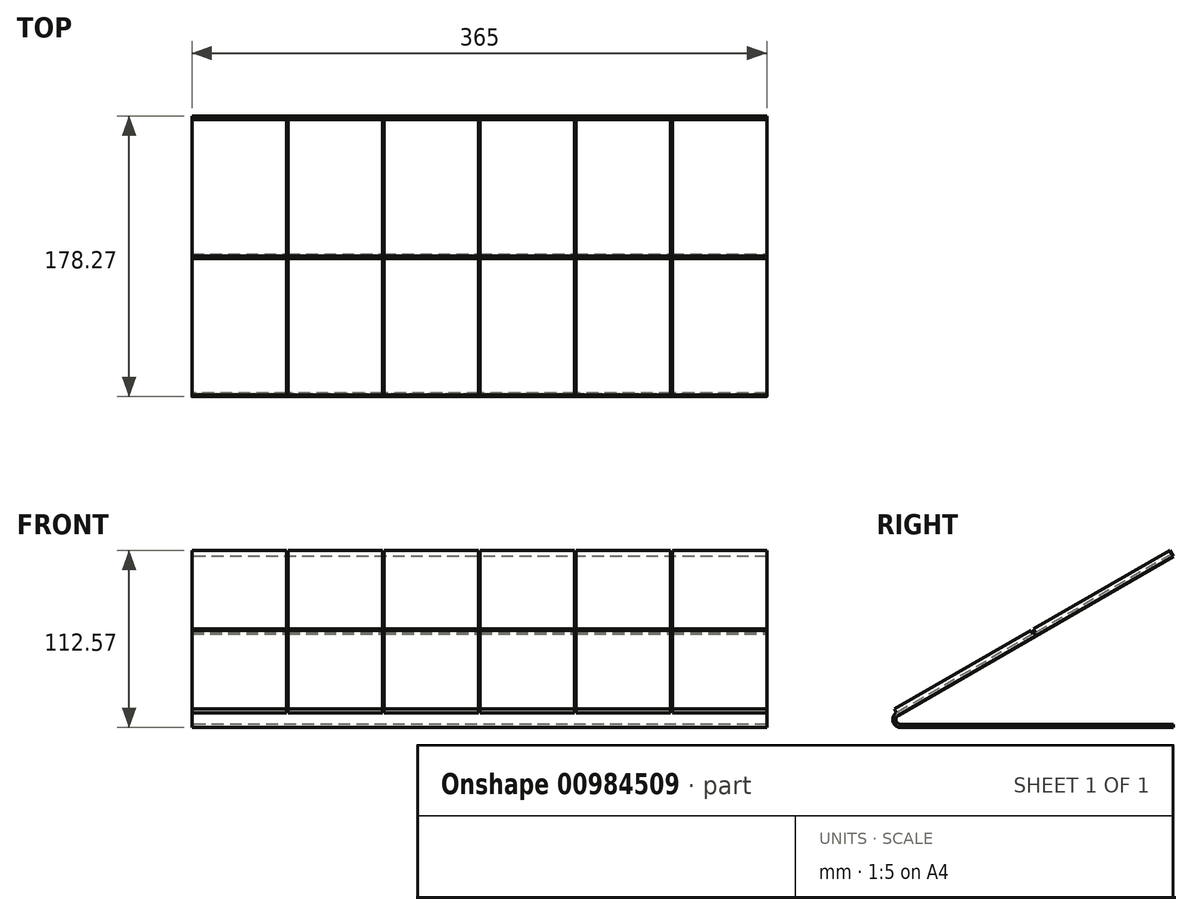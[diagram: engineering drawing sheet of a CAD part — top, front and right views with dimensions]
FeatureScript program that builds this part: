
annotation { "Feature Type Name" : "Feature", "Feature Type Description" : "" }
export const myFeature = defineFeature(function(context is Context, id is Id, definition is map)
    precondition{}
    {
        {
            var Q0;
            Q0=qCreatedBy(makeId("Right.planeOp"),FACE);
            var sketch = newSketch(context, id + "F0", { "sketchPlane" : qUnion([Q0])});
            skLineSegment(sketch, "E0", {"start": v(0, 2) * mm, "end": v(-184.46, 2) * mm});
            skLineSegment(sketch, "E1", {"start": v(-184.46, 2) * mm, "end": v(0, 108.5) * mm});
            skLineSegment(sketch, "E2", {"start": v(0, 108.5) * mm, "end": v(-1, 110.23) * mm});
            skLineSegment(sketch, "E3", {"start": v(-1, 110.23) * mm, "end": v(-191.93, 0) * mm});
            skLineSegment(sketch, "E4", {"start": v(-191.93, 0) * mm, "end": v(0, 0) * mm});
            skLineSegment(sketch, "E5", {"start": v(0, 0) * mm, "end": v(0, 2) * mm});
            skSolve(sketch);
        }
        {
            var Q0;
            Q0 = qSketchRegion(id + "F0", true);
            extrude(context, id + "F1", {"entities" : qUnion([Q0]), "depth" : 365 * mm, "offsetDistance" : 25 * mm});
        }
        {
            var Q0;
            Q0=makeQuery(id+"F1.opExtrude","SWEPT_EDGE",EDGE,{"disambiguationData":[OSD([sQuery(id+"F0.wireOp",EDGE,"E0"),sQuery(id+"F0.wireOp",EDGE,"E1")])]});
            fillet(context, id + "F2", {"entities" : qUnion([Q0]), "radius" : 3 * mm, "tangentPropagation" : true, "allowEdgeOverflow" : false});
        }
        {
            var Q0;
            Q0=makeQuery(id+"F1.opExtrude","SWEPT_EDGE",EDGE,{"disambiguationData":[OSD([sQuery(id+"F0.wireOp",EDGE,"E3"),sQuery(id+"F0.wireOp",EDGE,"E4")])]});
            fillet(context, id + "F3", {"entities" : qUnion([Q0]), "radius" : 5 * mm, "tangentPropagation" : true, "allowEdgeOverflow" : false});
        }
        {
            var Q0;
            Q0=makeQuery(id+"F1.opExtrude","SWEPT_FACE",FACE,{"disambiguationData":[OSD([sQuery(id+"F0.wireOp",EDGE,"E3")])]});
            var sketch = newSketch(context, id + "F4", { "sketchPlane" : qUnion([Q0])});
            skLineSegment(sketch, "E6.bottom", {"start": v(0, 54.25) * mm, "end": v(60, 54.25) * mm});
            skLineSegment(sketch, "E6.top", {"start": v(0, -45.75) * mm, "end": v(60, -45.75) * mm});
            skLineSegment(sketch, "E6.left", {"start": v(0, 54.25) * mm, "end": v(0, -45.75) * mm});
            skLineSegment(sketch, "E6.right", {"start": v(60, 54.25) * mm, "end": v(60, -45.75) * mm});
            skLineSegment(sketch, "E7.bottom", {"start": v(61, 54.25) * mm, "end": v(121, 54.25) * mm});
            skLineSegment(sketch, "E7.top", {"start": v(61, -45.75) * mm, "end": v(121, -45.75) * mm});
            skLineSegment(sketch, "E7.left", {"start": v(61, 54.25) * mm, "end": v(61, -45.75) * mm});
            skLineSegment(sketch, "E7.right", {"start": v(121, 54.25) * mm, "end": v(121, -45.75) * mm});
            skLineSegment(sketch, "E8.bottom", {"start": v(122, 54.25) * mm, "end": v(182, 54.25) * mm});
            skLineSegment(sketch, "E8.top", {"start": v(122, -45.75) * mm, "end": v(182, -45.75) * mm});
            skLineSegment(sketch, "E8.left", {"start": v(122, 54.25) * mm, "end": v(122, -45.75) * mm});
            skLineSegment(sketch, "E8.right", {"start": v(182, 54.25) * mm, "end": v(182, -45.75) * mm});
            skLineSegment(sketch, "E9.bottom", {"start": v(183, 54.25) * mm, "end": v(243, 54.25) * mm});
            skLineSegment(sketch, "E9.top", {"start": v(183, -45.75) * mm, "end": v(243, -45.75) * mm});
            skLineSegment(sketch, "E9.left", {"start": v(183, 54.25) * mm, "end": v(183, -45.75) * mm});
            skLineSegment(sketch, "E9.right", {"start": v(243, 54.25) * mm, "end": v(243, -45.75) * mm});
            skLineSegment(sketch, "E10.bottom", {"start": v(244, 54.25) * mm, "end": v(304, 54.25) * mm});
            skLineSegment(sketch, "E10.top", {"start": v(244, -45.75) * mm, "end": v(304, -45.75) * mm});
            skLineSegment(sketch, "E10.left", {"start": v(244, 54.25) * mm, "end": v(244, -45.75) * mm});
            skLineSegment(sketch, "E10.right", {"start": v(304, 54.25) * mm, "end": v(304, -45.75) * mm});
            skLineSegment(sketch, "E11.bottom", {"start": v(305, 54.25) * mm, "end": v(365, 54.25) * mm});
            skLineSegment(sketch, "E11.top", {"start": v(305, -45.75) * mm, "end": v(365, -45.75) * mm});
            skLineSegment(sketch, "E11.left", {"start": v(305, 54.25) * mm, "end": v(305, -45.75) * mm});
            skLineSegment(sketch, "E11.right", {"start": v(365, 54.25) * mm, "end": v(365, -45.75) * mm});
            skLineSegment(sketch, "E12.bottom", {"start": v(0, -47.55) * mm, "end": v(60, -47.55) * mm});
            skLineSegment(sketch, "E12.top", {"start": v(0, -147.55) * mm, "end": v(60, -147.55) * mm});
            skLineSegment(sketch, "E12.left", {"start": v(0, -47.55) * mm, "end": v(0, -147.55) * mm});
            skLineSegment(sketch, "E12.right", {"start": v(60, -47.55) * mm, "end": v(60, -147.55) * mm});
            skLineSegment(sketch, "E13.bottom", {"start": v(61, -47.55) * mm, "end": v(121, -47.55) * mm});
            skLineSegment(sketch, "E13.top", {"start": v(61, -147.55) * mm, "end": v(121, -147.55) * mm});
            skLineSegment(sketch, "E13.left", {"start": v(61, -47.55) * mm, "end": v(61, -147.55) * mm});
            skLineSegment(sketch, "E13.right", {"start": v(121, -47.55) * mm, "end": v(121, -147.55) * mm});
            skLineSegment(sketch, "E14.bottom", {"start": v(122, -47.55) * mm, "end": v(182, -47.55) * mm});
            skLineSegment(sketch, "E14.top", {"start": v(122, -147.55) * mm, "end": v(182, -147.55) * mm});
            skLineSegment(sketch, "E14.left", {"start": v(122, -47.55) * mm, "end": v(122, -147.55) * mm});
            skLineSegment(sketch, "E14.right", {"start": v(182, -47.55) * mm, "end": v(182, -147.55) * mm});
            skLineSegment(sketch, "E15.bottom", {"start": v(183, -47.55) * mm, "end": v(243, -47.55) * mm});
            skLineSegment(sketch, "E15.top", {"start": v(183, -147.55) * mm, "end": v(243, -147.55) * mm});
            skLineSegment(sketch, "E15.left", {"start": v(183, -47.55) * mm, "end": v(183, -147.55) * mm});
            skLineSegment(sketch, "E15.right", {"start": v(243, -47.55) * mm, "end": v(243, -147.55) * mm});
            skLineSegment(sketch, "E16.bottom", {"start": v(244, -47.55) * mm, "end": v(304, -47.55) * mm});
            skLineSegment(sketch, "E16.top", {"start": v(244, -147.55) * mm, "end": v(304, -147.55) * mm});
            skLineSegment(sketch, "E16.left", {"start": v(244, -47.55) * mm, "end": v(244, -147.55) * mm});
            skLineSegment(sketch, "E16.right", {"start": v(304, -47.55) * mm, "end": v(304, -147.55) * mm});
            skLineSegment(sketch, "E17.bottom", {"start": v(305, -47.55) * mm, "end": v(365, -47.55) * mm});
            skLineSegment(sketch, "E17.top", {"start": v(305, -147.55) * mm, "end": v(365, -147.55) * mm});
            skLineSegment(sketch, "E17.left", {"start": v(305, -47.55) * mm, "end": v(305, -147.55) * mm});
            skLineSegment(sketch, "E17.right", {"start": v(365, -47.55) * mm, "end": v(365, -147.55) * mm});
            skSolve(sketch);
        }
        {
            var Q0;
            Q0 = qSketchRegion(id + "F4", true);
            extrude(context, id + "F5", {"entities" : qUnion([Q0]), "operationType" : NewBodyOperationType.ADD, "depth" : 2.7 * mm, "offsetDistance" : 25 * mm});
        }
    });
